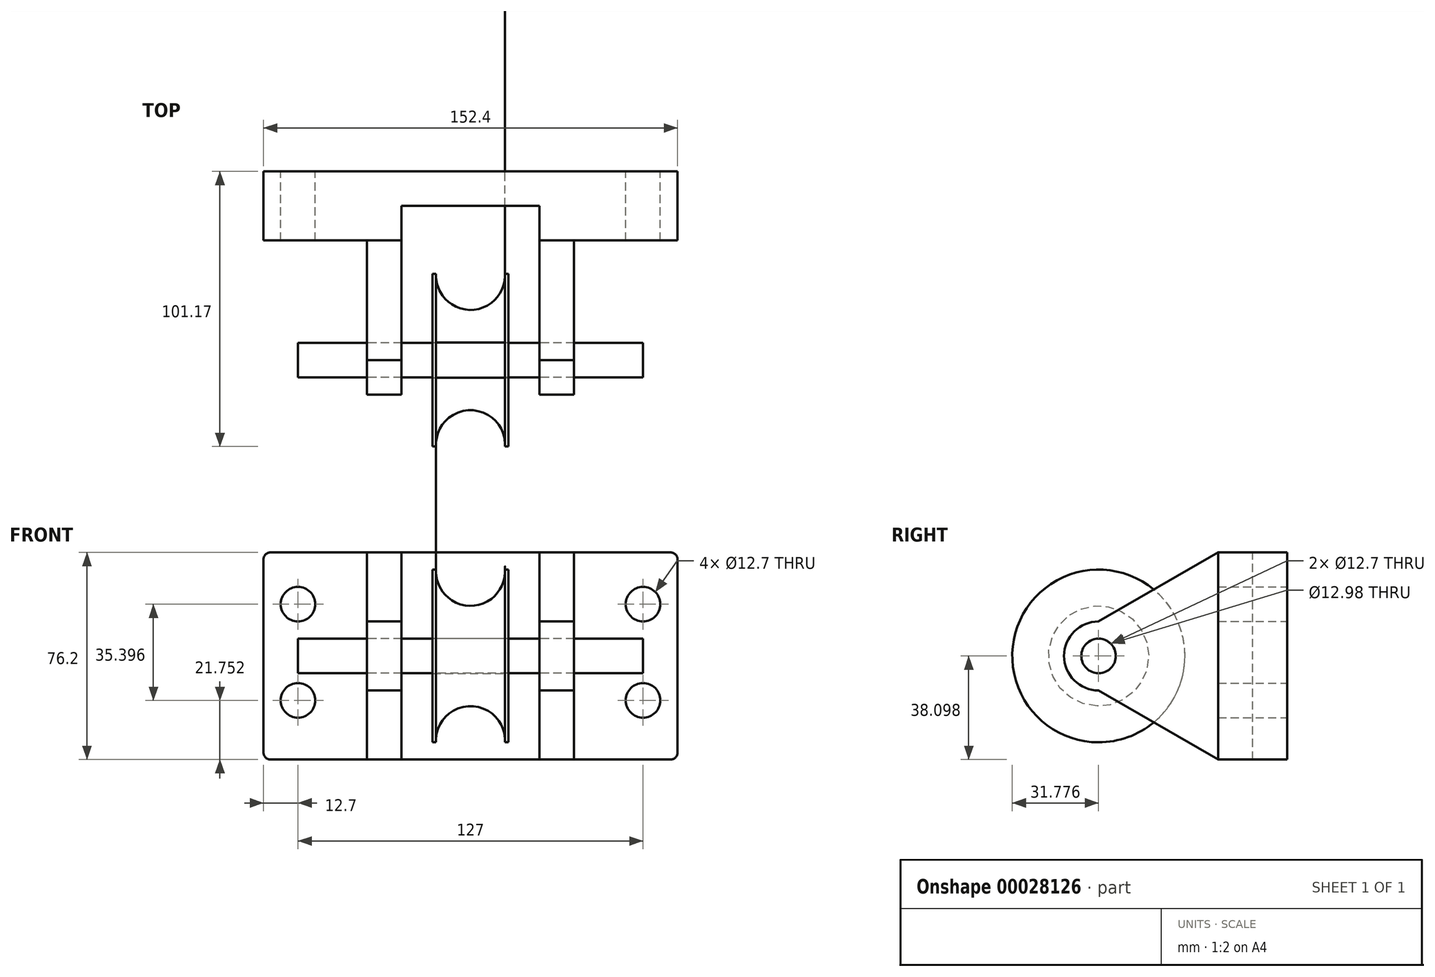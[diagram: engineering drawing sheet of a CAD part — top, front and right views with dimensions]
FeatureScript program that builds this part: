
annotation { "Feature Type Name" : "Feature", "Feature Type Description" : "" }
export const myFeature = defineFeature(function(context is Context, id is Id, definition is map)
    precondition{}
    {
        {
            var Q0;
            Q0=qCreatedBy(makeId("Front.planeOp"),FACE);
            var sketch = newSketch(context, id + "F0", { "sketchPlane" : qUnion([Q0])});
            skLineSegment(sketch, "E0.bottom", {"start": v(-76.2, 36.75) * mm, "end": v(76.2, 36.75) * mm});
            skLineSegment(sketch, "E0.top", {"start": v(-76.2, -39.45) * mm, "end": v(76.2, -39.45) * mm});
            skLineSegment(sketch, "E0.left", {"start": v(-76.2, 36.75) * mm, "end": v(-76.2, -39.45) * mm});
            skLineSegment(sketch, "E0.right", {"start": v(76.2, 36.75) * mm, "end": v(76.2, -39.45) * mm});
            skLineSegment(sketch, "E1", {"start": v(0, 36.75) * mm, "end": v(0, -39.45) * mm, "construction": true});
            skLineSegment(sketch, "E2", {"start": v(-76.2, 0) * mm, "end": v(76.2, 0) * mm, "construction": true});
            skCircle(sketch, "E3", {"center": v(-63.5, 17.7) * mm, "radius": 6.35 * mm});
            skCircle(sketch, "E4.MirrorC", {"center": v(-63.5, -17.7) * mm, "radius": 6.35 * mm});
            skCircle(sketch, "E5.MirrorC", {"center": v(63.5, 17.7) * mm, "radius": 6.35 * mm});
            skCircle(sketch, "E6.MirrorC", {"center": v(63.5, -17.7) * mm, "radius": 6.35 * mm});
            skSolve(sketch);
        }
        {
            var Q0;
            Q0=makeQuery(id+"F0.imprint","IMPRINT",FACE,{"disambiguationData":[TD([[makeQuery(id+"F0.imprint","IMPRINT",EDGE,{"derivedFrom":sQuery(id+"F0.wireOp",EDGE,"E0.bottom")}),-1.0]])]});
            extrude(context, id + "F1", {"entities" : qUnion([Q0]), "depth" : 12.7 * mm});
        }
        {
            var Q0;
            Q0=makeQuery(id+"F1.opExtrude","SWEPT_EDGE",EDGE,{"disambiguationData":[OSD([sQuery(id+"F0.wireOp",EDGE,"E0.top"),sQuery(id+"F0.wireOp",EDGE,"E0.right")])]});
            var Q1;
            Q1=makeQuery(id+"F1.opExtrude","SWEPT_EDGE",EDGE,{"disambiguationData":[OSD([sQuery(id+"F0.wireOp",EDGE,"E0.bottom"),sQuery(id+"F0.wireOp",EDGE,"E0.right")])]});
            var Q2;
            Q2=makeQuery(id+"F1.opExtrude","SWEPT_EDGE",EDGE,{"disambiguationData":[OSD([sQuery(id+"F0.wireOp",EDGE,"E0.top"),sQuery(id+"F0.wireOp",EDGE,"E0.left")])]});
            var Q3;
            Q3=makeQuery(id+"F1.opExtrude","SWEPT_EDGE",EDGE,{"disambiguationData":[OSD([sQuery(id+"F0.wireOp",EDGE,"E0.bottom"),sQuery(id+"F0.wireOp",EDGE,"E0.left")])]});
            fillet(context, id + "F2", {"entities" : qUnion([Q0, Q1, Q2, Q3]), "radius" : 2.54 * mm, "tangentPropagation" : true, "allowEdgeOverflow" : false});
        }
        {
            var Q0;
            Q0=makeQuery(id+"F1.opExtrude","CAP_FACE",FACE,{"disambiguationData":[OSD([sQuery(id+"F0.wireOp",EDGE,"E0.bottom"),sQuery(id+"F0.wireOp",EDGE,"E0.top"),sQuery(id+"F0.wireOp",EDGE,"E0.left"),sQuery(id+"F0.wireOp",EDGE,"E0.right"),sQuery(id+"F0.wireOp",EDGE,"E3"),sQuery(id+"F0.wireOp",EDGE,"E4.MirrorC"),sQuery(id+"F0.wireOp",EDGE,"E5.MirrorC"),sQuery(id+"F0.wireOp",EDGE,"E6.MirrorC")])],"isStart":false});
            var sketch = newSketch(context, id + "F3", { "sketchPlane" : qUnion([Q0])});
            skLineSegment(sketch, "E7.bottom", {"start": v(-76.2, 36.75) * mm, "end": v(-38.1, 36.75) * mm});
            skLineSegment(sketch, "E7.top", {"start": v(-76.2, -39.45) * mm, "end": v(-38.1, -39.45) * mm});
            skLineSegment(sketch, "E7.left", {"start": v(-76.2, 36.75) * mm, "end": v(-76.2, -39.45) * mm});
            skLineSegment(sketch, "E7.right", {"start": v(-38.1, 36.75) * mm, "end": v(-38.1, -39.45) * mm});
            skLineSegment(sketch, "E8.0", {"start": v(-73.66, 36.75) * mm, "end": v(73.66, 36.75) * mm});
            skSolve(sketch);
        }
        {
            var Q0;
            {var subQ8=sQuery(id+"F3.wireOp",EDGE,"E7.right");Q0=makeQuery(id+"F3.imprint","IMPRINT",FACE,{"disambiguationData":[TD([[makeQuery(id+"F3.imprint","IMPRINT",EDGE,{"derivedFrom":subQ8}),-1.0]])]});}
            extrude(context, id + "F4", {"entities" : qUnion([Q0]), "depth" : 12.7 * mm});
        }
        {
            var Q0;
            Q0=makeQuery(id+"F4.opExtrude","SWEPT_FACE",FACE,{"disambiguationData":[OSD([sQuery(id+"F3.wireOp",EDGE,"E7.right")])]});
            cPlane(context, id + "F5", {"entities" : qUnion([Q0]), "cplaneType" : CPlaneType.OFFSET, "offset" : 0 * mm, "width" : 152.4 * mm, "height" : 152.4 * mm});
        }
        {
            var Q0;
            Q0=qCreatedBy(id+"F5.planeOp",FACE);
            var sketch = newSketch(context, id + "F6", { "sketchPlane" : qUnion([Q0])});
            skLineSegment(sketch, "E9.0", {"start": v(-25.4, 36.75) * mm, "end": v(-25.4, -39.45) * mm});
            skLineSegment(sketch, "E10.0", {"start": v(-25.4, -39.45) * mm, "end": v(-12.7, -39.45) * mm});
            skLineSegment(sketch, "E11.0", {"start": v(-25.4, 36.75) * mm, "end": v(-12.7, 36.75) * mm});
            skLineSegment(sketch, "E12", {"start": v(-12.7, -39.45) * mm, "end": v(-12.7, 36.75) * mm});
            skLineSegment(sketch, "E13", {"start": v(-25.4, -39.45) * mm, "end": v(-69.4, -14.05) * mm});
            skLineSegment(sketch, "E14", {"start": v(-69.4, -14.05) * mm, "end": v(-69.4, 11.35) * mm});
            skLineSegment(sketch, "E15", {"start": v(-69.4, 11.35) * mm, "end": v(-25.4, 36.75) * mm});
            skCircle(sketch, "E16", {"center": v(-69.4, -1.35) * mm, "radius": 6.35 * mm});
            skCircle(sketch, "E17", {"center": v(-69.4, -1.35) * mm, "radius": 12.7 * mm});
            skSolve(sketch);
        }
        {
            var Q0;
            {var subQ1=sQuery(id+"F6.wireOp",EDGE,"E14");var subQ4=sQuery(id+"F6.wireOp",EDGE,"E16");var subQ6=makeQuery(id+"F6.imprint","INTERSECT",VERTEX,{"disambiguationData":[OD(0.0)],"derivedFrom":[subQ1,subQ4]});Q0=makeQuery(id+"F6.imprint","IMPRINT",FACE,{"disambiguationData":[TD([[makeQuery(id+"F6.imprint","IMPRINT",EDGE,{"disambiguationData":[TD([[subQ6,1.0]])],"derivedFrom":subQ4}),-1.0]])]});}
            var Q1;
            Q1=makeQuery(id+"F6.imprint","IMPRINT",FACE,{"disambiguationData":[TD([[makeQuery(id+"F6.imprint","IMPRINT",EDGE,{"derivedFrom":sQuery(id+"F6.wireOp",EDGE,"E9.0")}),-1.0]])]});
            var Q2;
            {var subQ1=sQuery(id+"F6.wireOp",EDGE,"E14");var subQ4=sQuery(id+"F6.wireOp",EDGE,"E16");var subQ6=makeQuery(id+"F6.imprint","INTERSECT",VERTEX,{"disambiguationData":[OD(0.0)],"derivedFrom":[subQ1,subQ4]});Q2=makeQuery(id+"F6.imprint","IMPRINT",FACE,{"disambiguationData":[TD([[makeQuery(id+"F6.imprint","IMPRINT",EDGE,{"disambiguationData":[TD([[subQ6,-1.0]])],"derivedFrom":subQ4}),-1.0]])]});}
            var Q3;
            Q3=makeQuery(id+"F6.imprint","IMPRINT",FACE,{"disambiguationData":[TD([[makeQuery(id+"F6.imprint","IMPRINT",EDGE,{"derivedFrom":sQuery(id+"F6.wireOp",EDGE,"E9.0")}),1.0]])]});
            extrude(context, id + "F7", {"entities" : qUnion([Q0, Q1, Q2, Q3]), "depth" : 12.7 * mm});
        }
        {
            var Q0;
            Q0=makeQuery(id+"F7.opExtrude","SWEPT_BODY",BODY,{"disambiguationData":[OSD([sQuery(id+"F6.wireOp",EDGE,"E10.0"),sQuery(id+"F6.wireOp",EDGE,"E11.0"),sQuery(id+"F6.wireOp",EDGE,"E12"),sQuery(id+"F6.wireOp",EDGE,"E13"),sQuery(id+"F6.wireOp",EDGE,"E15"),sQuery(id+"F6.wireOp",EDGE,"E16"),sQuery(id+"F6.wireOp",EDGE,"E17")])]});
            var Q1;
            Q1=makeQuery(id+"F4.opExtrude","SWEPT_BODY",BODY,{"disambiguationData":[OSD([sQuery(id+"F0.wireOp",EDGE,"E0.bottom"),sQuery(id+"F0.wireOp",EDGE,"E0.top"),sQuery(id+"F0.wireOp",EDGE,"E0.left"),sQuery(id+"F0.wireOp",EDGE,"E0.right"),sQuery(id+"F0.wireOp",EDGE,"E3"),sQuery(id+"F0.wireOp",EDGE,"E4.MirrorC"),sQuery(id+"F0.wireOp",EDGE,"E5.MirrorC"),sQuery(id+"F0.wireOp",EDGE,"E6.MirrorC"),sQuery(id+"F3.wireOp",EDGE,"E7.bottom"),sQuery(id+"F3.wireOp",EDGE,"E7.top"),sQuery(id+"F3.wireOp",EDGE,"E7.left"),sQuery(id+"F3.wireOp",EDGE,"E7.right")])]});
            var Q2;
            Q2=qCreatedBy(makeId("Right.planeOp"),FACE);
            mirror(context, id + "F8", {"operationType" : NewBodyOperationType.ADD, "entities" : qUnion([Q0, Q1]), "mirrorPlane" : qUnion([Q2])});
        }
        {
            var Q0;
            Q0=qCreatedBy(id+"F5.planeOp",FACE);
            var sketch = newSketch(context, id + "F9", { "sketchPlane" : qUnion([Q0])});
            skCircle(sketch, "E18.0", {"center": v(-69.4, -1.35) * mm, "radius": 6.35 * mm});
            skSolve(sketch);
        }
        {
            var Q0;
            Q0 = qSketchRegion(id + "F9", true);
            extrude(context, id + "F10", {"entities" : qUnion([Q0]), "depth" : 101.6 * mm, "hasSecondDirection" : true, "secondDirectionOppositeDirection" : true, "secondDirectionDepth" : 25.4 * mm});
        }
        {
            var Q0;
            Q0=qCreatedBy(makeId("Top.planeOp"),FACE);
            var sketch = newSketch(context, id + "F11", { "sketchPlane" : qUnion([Q0])});
            skLineSegment(sketch, "E19", {"start": v(63.5, -75.74) * mm, "end": v(-63.5, -75.74) * mm, "construction": true});
            skLineSegment(sketch, "E20", {"start": v(-12.7, -99.88) * mm, "end": v(-12.7, -101.14) * mm});
            skLineSegment(sketch, "E21", {"start": v(12.7, -101.14) * mm, "end": v(12.7, -99.88) * mm});
            skArc(sketch, "E22", {"start": v(12.7, -101.14) * mm, "mid": v(0, -87.8) * mm, "end": v(-12.7, -101.14) * mm});
            skLineSegment(sketch, "E23", {"start": v(-12.7, -75.74) * mm, "end": v(12.7, -75.74) * mm});
            skLineSegment(sketch, "E24.bottom", {"start": v(-12.7, -101.14) * mm, "end": v(-13.97, -101.14) * mm});
            skLineSegment(sketch, "E24.top", {"start": v(-12.7, -75.74) * mm, "end": v(-13.97, -75.74) * mm});
            skLineSegment(sketch, "E24.left", {"start": v(-12.7, -101.14) * mm, "end": v(-12.7, -99.88) * mm});
            skLineSegment(sketch, "E24.right", {"start": v(-13.97, -101.14) * mm, "end": v(-13.97, -75.74) * mm});
            skLineSegment(sketch, "E25.MirrorCS", {"start": v(12.7, -101.14) * mm, "end": v(13.97, -101.14) * mm});
            skLineSegment(sketch, "E26.MirrorCS", {"start": v(13.97, -101.14) * mm, "end": v(13.97, -75.74) * mm});
            skLineSegment(sketch, "E27.MirrorCS", {"start": v(12.7, -75.74) * mm, "end": v(13.97, -75.74) * mm});
            skSolve(sketch);
        }
        {
            var Q0;
            Q0=makeQuery(id+"F11.imprint","IMPRINT",FACE,{"disambiguationData":[TD([[makeQuery(id+"F11.imprint","IMPRINT",EDGE,{"derivedFrom":sQuery(id+"F11.wireOp",EDGE,"E23")}),-1.0]])]});
            var Q1;
            Q1=makeQuery(id+"F10.opExtrude","SWEPT_FACE",FACE,{"disambiguationData":[OSD([sQuery(id+"F9.wireOp",EDGE,"E18.0")])]});
            revolve(context, id + "F12", {"entities" : qUnion([Q0]), "axis" : qUnion([Q1]), "revolveType" : RevolveType.FULL});
        }
    });
